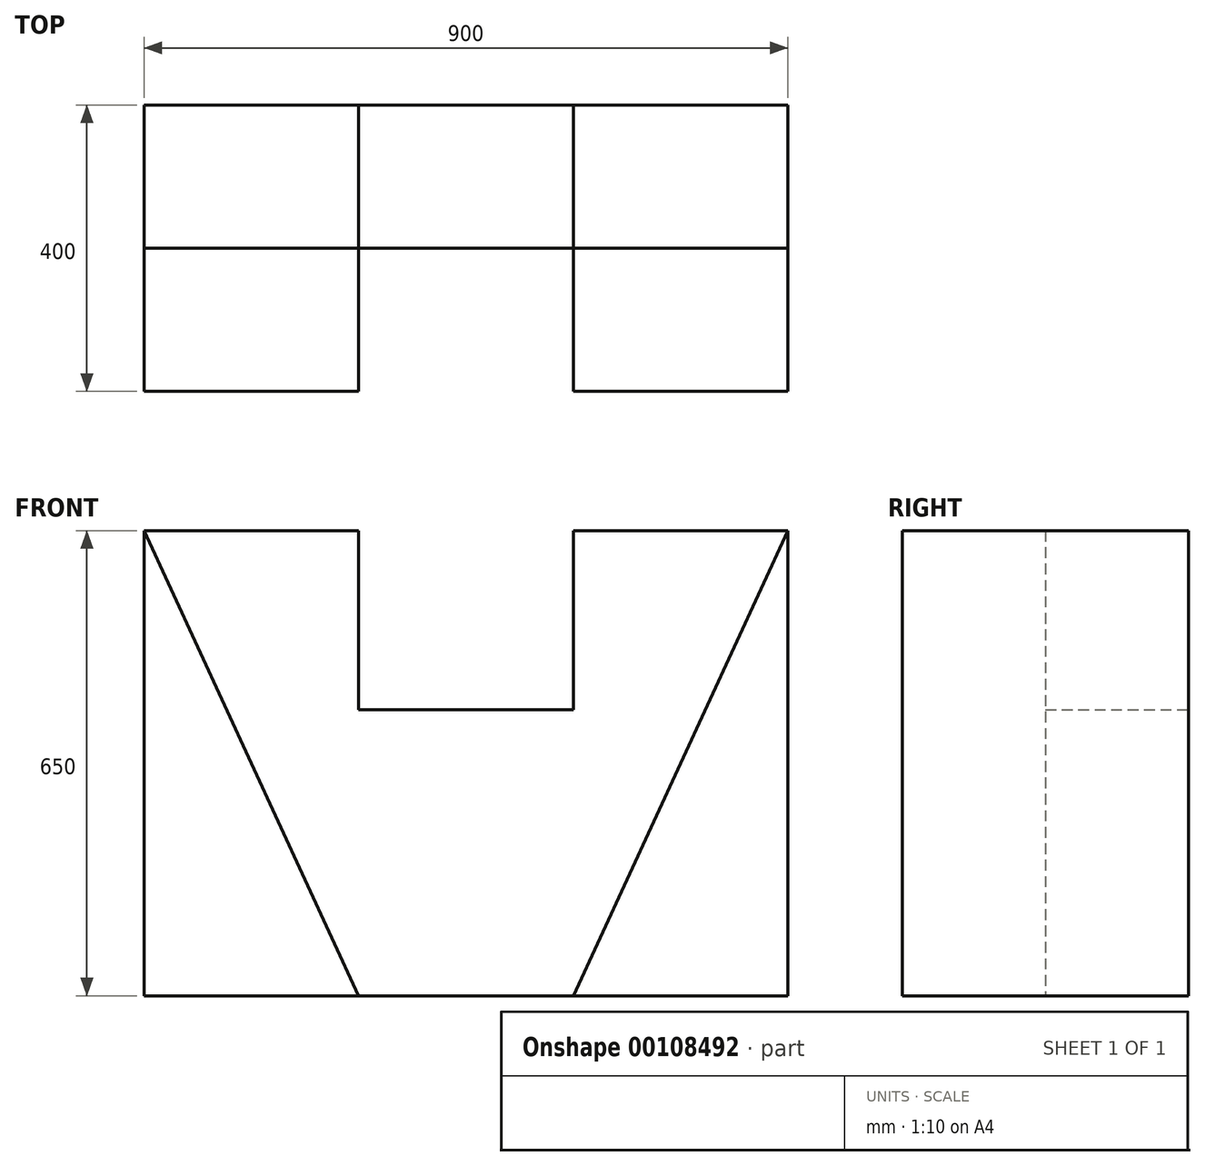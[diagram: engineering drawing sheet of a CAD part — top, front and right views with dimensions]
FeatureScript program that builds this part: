
annotation { "Feature Type Name" : "Feature", "Feature Type Description" : "" }
export const myFeature = defineFeature(function(context is Context, id is Id, definition is map)
    precondition{}
    {
        {
            var Q0;
            Q0=qCreatedBy(makeId("Front.planeOp"),FACE);
            var sketch = newSketch(context, id + "F0", { "sketchPlane" : qUnion([Q0])});
            skLineSegment(sketch, "E0.bottom", {"start": v(450, -325) * mm, "end": v(-450, -325) * mm});
            skLineSegment(sketch, "E0.top", {"start": v(450, 325) * mm, "end": v(150, 325) * mm});
            skLineSegment(sketch, "E0.left", {"start": v(450, -325) * mm, "end": v(450, 325) * mm});
            skLineSegment(sketch, "E0.right", {"start": v(-450, -325) * mm, "end": v(-450, 325) * mm});
            skPoint(sketch, "E0.middle", {"position": v(0, 0) * mm});
            skLineSegment(sketch, "E1.top", {"start": v(150, 75) * mm, "end": v(-150, 75) * mm});
            skLineSegment(sketch, "E1.left", {"start": v(150, 325) * mm, "end": v(150, 75) * mm});
            skLineSegment(sketch, "E1.right", {"start": v(-150, 325) * mm, "end": v(-150, 75) * mm});
            skPoint(sketch, "E1.middle", {"position": v(0, 325) * mm});
            skPoint(sketch, "E2.orphan", {"position": v(150, 575) * mm});
            skPoint(sketch, "E3.orphan", {"position": v(-150, 575) * mm});
            skLineSegment(sketch, "E4.trimOffspring", {"start": v(-150, 325) * mm, "end": v(-450, 325) * mm});
            skSolve(sketch);
        }
        {
            var Q0;
            Q0 = qSketchRegion(id + "F0", true);
            extrude(context, id + "F1", {"entities" : qUnion([Q0]), "depth" : 200 * mm});
        }
        {
            var Q0;
            Q0=makeQuery(id+"F1.opExtrude","CAP_FACE",FACE,{"disambiguationData":[OSD([sQuery(id+"F0.wireOp",EDGE,"E0.bottom"),sQuery(id+"F0.wireOp",EDGE,"E0.top"),sQuery(id+"F0.wireOp",EDGE,"E0.left"),sQuery(id+"F0.wireOp",EDGE,"E0.right"),sQuery(id+"F0.wireOp",EDGE,"E1.top"),sQuery(id+"F0.wireOp",EDGE,"E1.left"),sQuery(id+"F0.wireOp",EDGE,"E1.right"),sQuery(id+"F0.wireOp",EDGE,"E4.trimOffspring")])],"isStart":false});
            var sketch = newSketch(context, id + "F2", { "sketchPlane" : qUnion([Q0])});
            skLineSegment(sketch, "E5", {"start": v(-450, 325) * mm, "end": v(-150, -325) * mm});
            skLineSegment(sketch, "E6", {"start": v(-150, -325) * mm, "end": v(-450, -325) * mm});
            skLineSegment(sketch, "E7", {"start": v(-450, -325) * mm, "end": v(-450, 325) * mm});
            skLineSegment(sketch, "E8", {"start": v(450, 325) * mm, "end": v(150, -325) * mm});
            skLineSegment(sketch, "E9", {"start": v(150, -325) * mm, "end": v(450, -325) * mm});
            skLineSegment(sketch, "E10", {"start": v(450, -325) * mm, "end": v(450, 325) * mm});
            skSolve(sketch);
        }
        {
            var Q0;
            Q0=makeQuery(id+"F2.imprint","IMPRINT",FACE,{"disambiguationData":[TD([[makeQuery(id+"F2.imprint","IMPRINT",EDGE,{"derivedFrom":sQuery(id+"F2.wireOp",EDGE,"E5")}),-1.0]])]});
            var Q1;
            Q1=makeQuery(id+"F2.imprint","IMPRINT",FACE,{"disambiguationData":[TD([[makeQuery(id+"F2.imprint","IMPRINT",EDGE,{"derivedFrom":sQuery(id+"F2.wireOp",EDGE,"E8")}),1.0]])]});
            extrude(context, id + "F3", {"entities" : qUnion([Q0, Q1]), "operationType" : NewBodyOperationType.ADD, "depth" : 200 * mm});
        }
    });
